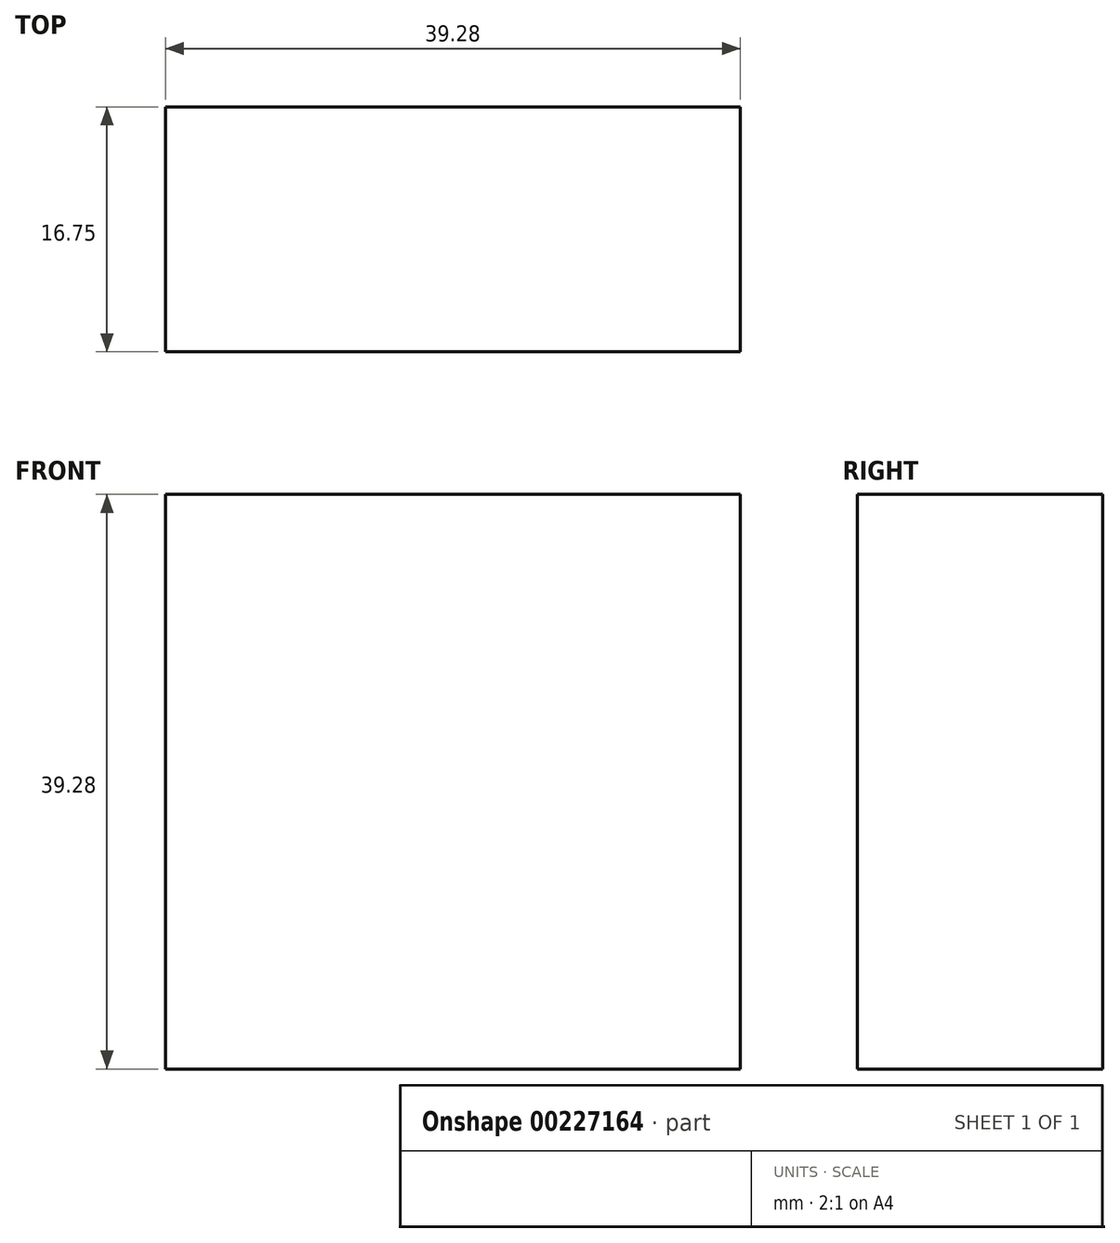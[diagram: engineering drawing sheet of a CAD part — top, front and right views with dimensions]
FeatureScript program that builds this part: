
annotation { "Feature Type Name" : "Feature", "Feature Type Description" : "" }
export const myFeature = defineFeature(function(context is Context, id is Id, definition is map)
    precondition{}
    {
        {
            var Q0;
            Q0=qCreatedBy(makeId("Front.planeOp"),FACE);
            var sketch = newSketch(context, id + "F0", { "sketchPlane" : qUnion([Q0])});
            skLineSegment(sketch, "E0.bottom", {"start": v(19.64, -19.64) * mm, "end": v(-19.64, -19.64) * mm});
            skLineSegment(sketch, "E0.top", {"start": v(19.64, 19.64) * mm, "end": v(-19.64, 19.64) * mm});
            skLineSegment(sketch, "E0.left", {"start": v(19.64, -19.64) * mm, "end": v(19.64, 19.64) * mm});
            skLineSegment(sketch, "E0.right", {"start": v(-19.64, -19.64) * mm, "end": v(-19.64, 19.64) * mm});
            skPoint(sketch, "E0.middle", {"position": v(0, 0) * mm});
            skSolve(sketch);
        }
        {
            var Q0;
            Q0 = qSketchRegion(id + "F0", true);
            extrude(context, id + "F1", {"entities" : qUnion([Q0]), "depth" : 16.75 * mm});
        }
    });
